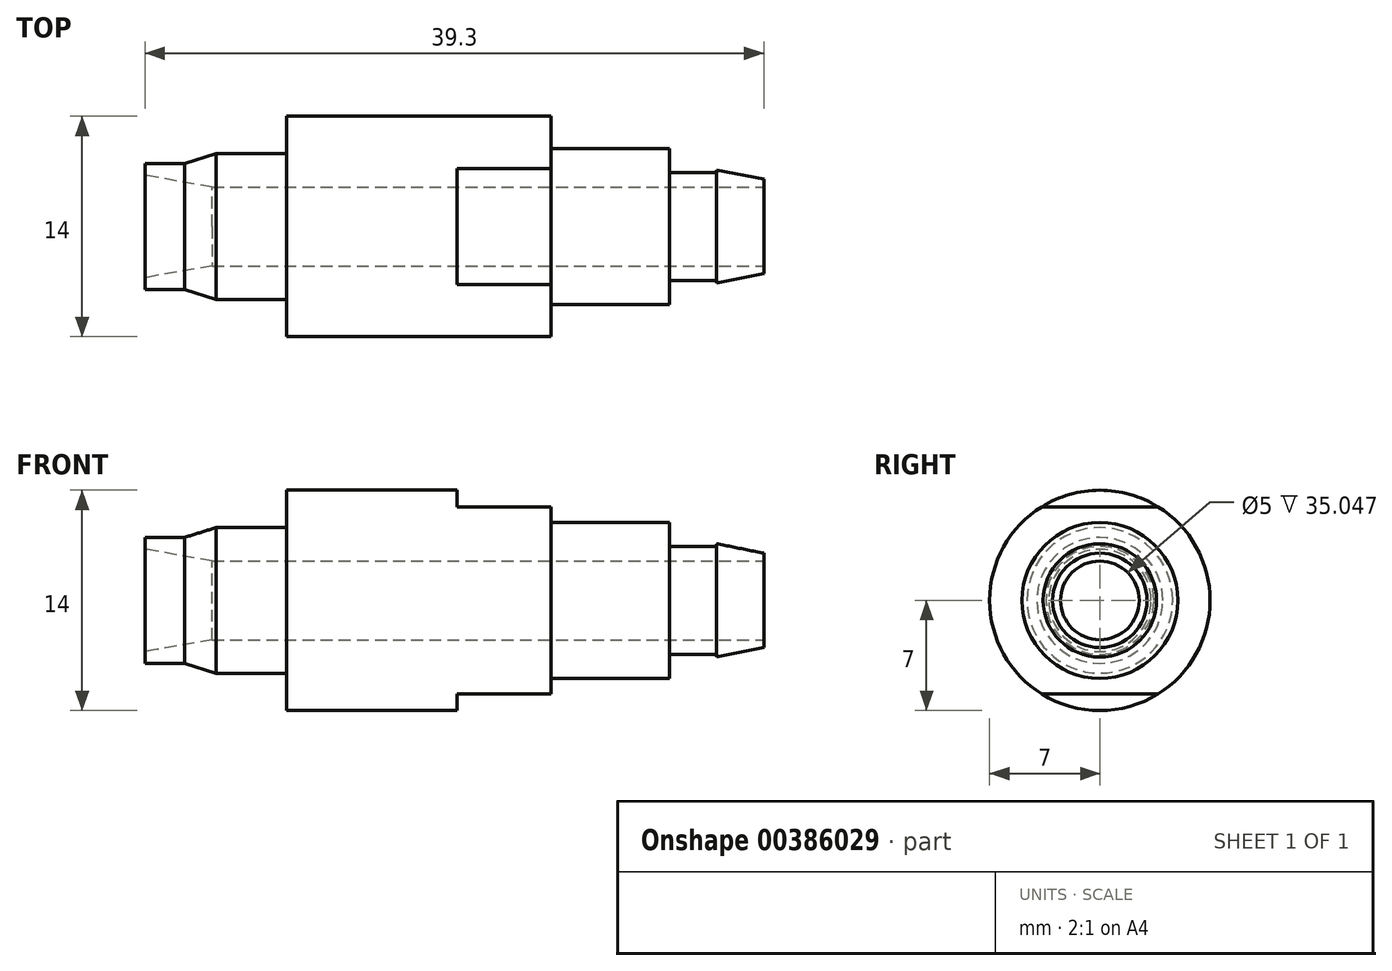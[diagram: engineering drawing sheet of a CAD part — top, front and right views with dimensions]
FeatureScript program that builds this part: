
annotation { "Feature Type Name" : "Feature", "Feature Type Description" : "" }
export const myFeature = defineFeature(function(context is Context, id is Id, definition is map)
    precondition{}
    {
        {
            var Q0;
            Q0=qCreatedBy(makeId("Front.planeOp"),FACE);
            var sketch = newSketch(context, id + "F0", { "sketchPlane" : qUnion([Q0])});
            skLineSegment(sketch, "E0", {"start": v(0, 0) * mm, "end": v(16.8, 0) * mm});
            skLineSegment(sketch, "E1", {"start": v(16.8, 7) * mm, "end": v(16.8, -7) * mm});
            skLineSegment(sketch, "E2", {"start": v(-61.16, 0) * mm, "end": v(71.68, 0) * mm});
            skLineSegment(sketch, "E3", {"start": v(24.3, 4.95) * mm, "end": v(24.3, -4.95) * mm});
            skLineSegment(sketch, "E4", {"start": v(27.3, 3.43) * mm, "end": v(27.3, -3.42) * mm});
            skLineSegment(sketch, "E5", {"start": v(30.3, 3) * mm, "end": v(30.3, -3) * mm});
            skLineSegment(sketch, "E6", {"start": v(0, 7) * mm, "end": v(0, -7) * mm});
            skLineSegment(sketch, "E7", {"start": v(-4.5, 4.62) * mm, "end": v(-4.5, -4.62) * mm});
            skLineSegment(sketch, "E8", {"start": v(-6.5, 4) * mm, "end": v(-6.5, -4) * mm});
            skLineSegment(sketch, "E9", {"start": v(-9, 4) * mm, "end": v(-9, -4) * mm});
            skLineSegment(sketch, "E10", {"start": v(-9, 4) * mm, "end": v(-6.5, 4) * mm});
            skLineSegment(sketch, "E11", {"start": v(-6.5, 4) * mm, "end": v(-4.5, 4.62) * mm});
            skLineSegment(sketch, "E12", {"start": v(-4.5, 4.62) * mm, "end": v(0, 4.63) * mm});
            skLineSegment(sketch, "E13", {"start": v(0, 7) * mm, "end": v(16.8, 7) * mm});
            skLineSegment(sketch, "E14", {"start": v(24.3, 4.95) * mm, "end": v(16.8, 4.95) * mm});
            skLineSegment(sketch, "E15", {"start": v(27.3, 3.43) * mm, "end": v(24.3, 3.43) * mm});
            skLineSegment(sketch, "E16", {"start": v(27.3, 0) * mm, "end": v(27.3, 3.6) * mm});
            skLineSegment(sketch, "E17", {"start": v(27.3, 3.6) * mm, "end": v(30.3, 3) * mm});
            skSolve(sketch);
        }
        {
            var Q0;
            {var subQ5=sQuery(id+"F0.wireOp",EDGE,"x26fzHlS-crBZ-tJss-jCmj-51uunG6Zshck");Q0=makeQuery(id+"F0.imprint","IMPRINT",FACE,{"disambiguationData":[TD([[makeQuery(id+"F0.imprint","IMPRINT",EDGE,{"derivedFrom":subQ5}),1.0]])]});}
            var Q1;
            {var subQ5=sQuery(id+"F0.wireOp",EDGE,"E10");Q1=makeQuery(id+"F0.imprint","IMPRINT",FACE,{"disambiguationData":[TD([[makeQuery(id+"F0.imprint","IMPRINT",EDGE,{"derivedFrom":subQ5}),-1.0]])]});}
            var Q2;
            {var subQ0=sQuery(id+"F0.wireOp",EDGE,"E13");Q2=makeQuery(id+"F0.imprint","IMPRINT",FACE,{"disambiguationData":[TD([[makeQuery(id+"F0.imprint","IMPRINT",EDGE,{"derivedFrom":subQ0}),-1.0]])]});}
            var Q3;
            {var subQ5=sQuery(id+"F0.wireOp",EDGE,"E15");Q3=makeQuery(id+"F0.imprint","IMPRINT",FACE,{"disambiguationData":[TD([[makeQuery(id+"F0.imprint","IMPRINT",EDGE,{"derivedFrom":subQ5}),1.0]])]});}
            var Q4;
            {var subQ0=sQuery(id+"F0.wireOp",EDGE,"E14");Q4=makeQuery(id+"F0.imprint","IMPRINT",FACE,{"disambiguationData":[TD([[makeQuery(id+"F0.imprint","IMPRINT",EDGE,{"derivedFrom":subQ0}),1.0]])]});}
            var Q5;
            {var subQ5=sQuery(id+"F0.wireOp",EDGE,"r0wMiud3-wyZs-0Lxd-goAT-lmOCEWkms3Fi");Q5=makeQuery(id+"F0.imprint","IMPRINT",FACE,{"disambiguationData":[TD([[makeQuery(id+"F0.imprint","IMPRINT",EDGE,{"derivedFrom":subQ5}),1.0]])]});}
            var Q6;
            {var subQ5=sQuery(id+"F0.wireOp",EDGE,"E11");Q6=makeQuery(id+"F0.imprint","IMPRINT",FACE,{"disambiguationData":[TD([[makeQuery(id+"F0.imprint","IMPRINT",EDGE,{"derivedFrom":subQ5}),-1.0]])]});}
            var Q7;
            {var subQ5=sQuery(id+"F0.wireOp",EDGE,"E12");Q7=makeQuery(id+"F0.imprint","IMPRINT",FACE,{"disambiguationData":[TD([[makeQuery(id+"F0.imprint","IMPRINT",EDGE,{"derivedFrom":subQ5}),-1.0]])]});}
            var Q8;
            {var subQ2=sQuery(id+"F0.wireOp",EDGE,"E17");Q8=makeQuery(id+"F0.imprint","IMPRINT",FACE,{"disambiguationData":[TD([[makeQuery(id+"F0.imprint","IMPRINT",EDGE,{"derivedFrom":subQ2}),-1.0]])]});}
            var Q9;
            Q9=sQuery(id+"F0.wireOp",EDGE,"E2");
            revolve(context, id + "F1", {"surfaceOperationType" : NewSurfaceOperationType.NEW, "entities" : qUnion([Q0, Q1, Q2, Q3, Q4, Q5, Q6, Q7, Q8]), "axis" : qUnion([Q9]), "revolveType" : RevolveType.FULL});
        }
        {
            var Q0;
            Q0=makeQuery(id+"F1.opRevolve","SWEPT_FACE",FACE,{"disambiguationData":[OSD([sQuery(id+"F0.wireOp",EDGE,"E1")])]});
            var sketch = newSketch(context, id + "F2", { "sketchPlane" : qUnion([Q0])});
            skLineSegment(sketch, "E18.bottom", {"start": v(12.5, -5.95) * mm, "end": v(-12.5, -5.95) * mm});
            skLineSegment(sketch, "E18.top", {"start": v(12.5, 5.95) * mm, "end": v(-12.5, 5.95) * mm});
            skLineSegment(sketch, "E18.left", {"start": v(12.5, -5.95) * mm, "end": v(12.5, 5.95) * mm});
            skLineSegment(sketch, "E18.right", {"start": v(-12.5, -5.95) * mm, "end": v(-12.5, 5.95) * mm});
            skPoint(sketch, "E18.middle", {"position": v(0, 0) * mm});
            skLineSegment(sketch, "E19.bottom", {"start": v(12.5, -12.41) * mm, "end": v(-12.5, -12.41) * mm});
            skLineSegment(sketch, "E19.top", {"start": v(12.5, 12.41) * mm, "end": v(-12.5, 12.41) * mm});
            skLineSegment(sketch, "E19.left", {"start": v(12.5, -12.41) * mm, "end": v(12.5, 12.41) * mm});
            skLineSegment(sketch, "E19.right", {"start": v(-12.5, -12.41) * mm, "end": v(-12.5, 12.41) * mm});
            skSolve(sketch);
        }
        {
            var Q0;
            {var subQ0=sQuery(id+"F2.wireOp",EDGE,"E18.top");var subQ1=makeQuery(id+"F1.opRevolve","SWEPT_EDGE",EDGE,{"disambiguationData":[OSD([sQuery(id+"F0.wireOp",EDGE,"E1"),sQuery(id+"F0.wireOp",EDGE,"E13")])]});var subQ2=makeQuery(id+"F2.imprint","INTERSECT",VERTEX,{"disambiguationData":[OD(0.0)],"derivedFrom":[subQ1,subQ0]});Q0=makeQuery(id+"F2.imprint","IMPRINT",FACE,{"disambiguationData":[TD([[makeQuery(id+"F2.imprint","IMPRINT",EDGE,{"disambiguationData":[TD([[subQ2,-1.0]])],"derivedFrom":subQ0}),-1.0]])]});}
            var Q1;
            {var subQ0=sQuery(id+"F2.wireOp",EDGE,"E18.bottom");var subQ1=makeQuery(id+"F1.opRevolve","SWEPT_EDGE",EDGE,{"disambiguationData":[OSD([sQuery(id+"F0.wireOp",EDGE,"E1"),sQuery(id+"F0.wireOp",EDGE,"E13")])]});var subQ2=makeQuery(id+"F2.imprint","INTERSECT",VERTEX,{"disambiguationData":[OD(0.0)],"derivedFrom":[subQ1,subQ0]});Q1=makeQuery(id+"F2.imprint","IMPRINT",FACE,{"disambiguationData":[TD([[makeQuery(id+"F2.imprint","IMPRINT",EDGE,{"disambiguationData":[TD([[subQ2,-1.0]])],"derivedFrom":subQ0}),1.0]])]});}
            extrude(context, id + "F3", {"entities" : qUnion([Q0, Q1]), "operationType" : NewBodyOperationType.REMOVE, "oppositeDirection" : true, "depth" : 6 * mm, "offsetDistance" : 25 * mm});
        }
        {
            var Q0;
            Q0=makeQuery(id+"F1.opRevolve","SWEPT_FACE",FACE,{"disambiguationData":[OSD([sQuery(id+"F0.wireOp",EDGE,"E9")])]});
            cPlane(context, id + "F4", {"entities" : qUnion([Q0]), "cplaneType" : CPlaneType.OFFSET, "offset" : 0 * mm, "oppositeDirection" : true, "width" : 150 * mm, "height" : 150 * mm});
        }
        {
            var Q0;
            Q0=makeQuery(id+"F1.opRevolve","SWEPT_FACE",FACE,{"disambiguationData":[OSD([sQuery(id+"F0.wireOp",EDGE,"E16")])]});
            var sketch = newSketch(context, id + "F5", { "sketchPlane" : qUnion([Q0])});
            skCircle(sketch, "E20", {"center": v(0, 0) * mm, "radius": 2.5 * mm});
            skSolve(sketch);
        }
        {
            var Q0;
            Q0=makeQuery(id+"F5.imprint","IMPRINT",FACE,{"disambiguationData":[TD([[makeQuery(id+"F5.imprint","IMPRINT",EDGE,{"derivedFrom":sQuery(id+"F5.wireOp",EDGE,"E20")}),1.0]])]});
            extrude(context, id + "F6", {"entities" : qUnion([Q0]), "operationType" : NewBodyOperationType.REMOVE, "endBound" : BoundingType.THROUGH_ALL, "depth" : 50 * mm, "offsetDistance" : 25 * mm, "hasSecondDirection" : true, "secondDirectionBound" : SecondDirectionBoundingType.THROUGH_ALL, "secondDirectionOppositeDirection" : true, "secondDirectionDepth" : 25 * mm});
        }
        {
            var Q0;
            Q0=qCreatedBy(id+"F4.planeOp",FACE);
            var sketch = newSketch(context, id + "F7", { "sketchPlane" : qUnion([Q0])});
            skCircle(sketch, "E21", {"center": v(0, 0) * mm, "radius": 3.25 * mm});
            skSolve(sketch);
        }
        {
            var Q0;
            Q0 = qSketchRegion(id + "F7", true);
            extrude(context, id + "F8", {"entities" : qUnion([Q0]), "operationType" : NewBodyOperationType.REMOVE, "oppositeDirection" : true, "depth" : 20 * mm, "offsetDistance" : 25 * mm, "hasDraft" : true, "draftAngle" : 10 * degree, "draftPullDirection" : true, "hasSecondDirection" : true, "secondDirectionOppositeDirection" : false, "secondDirectionDepth" : 25 * mm});
        }
    });
